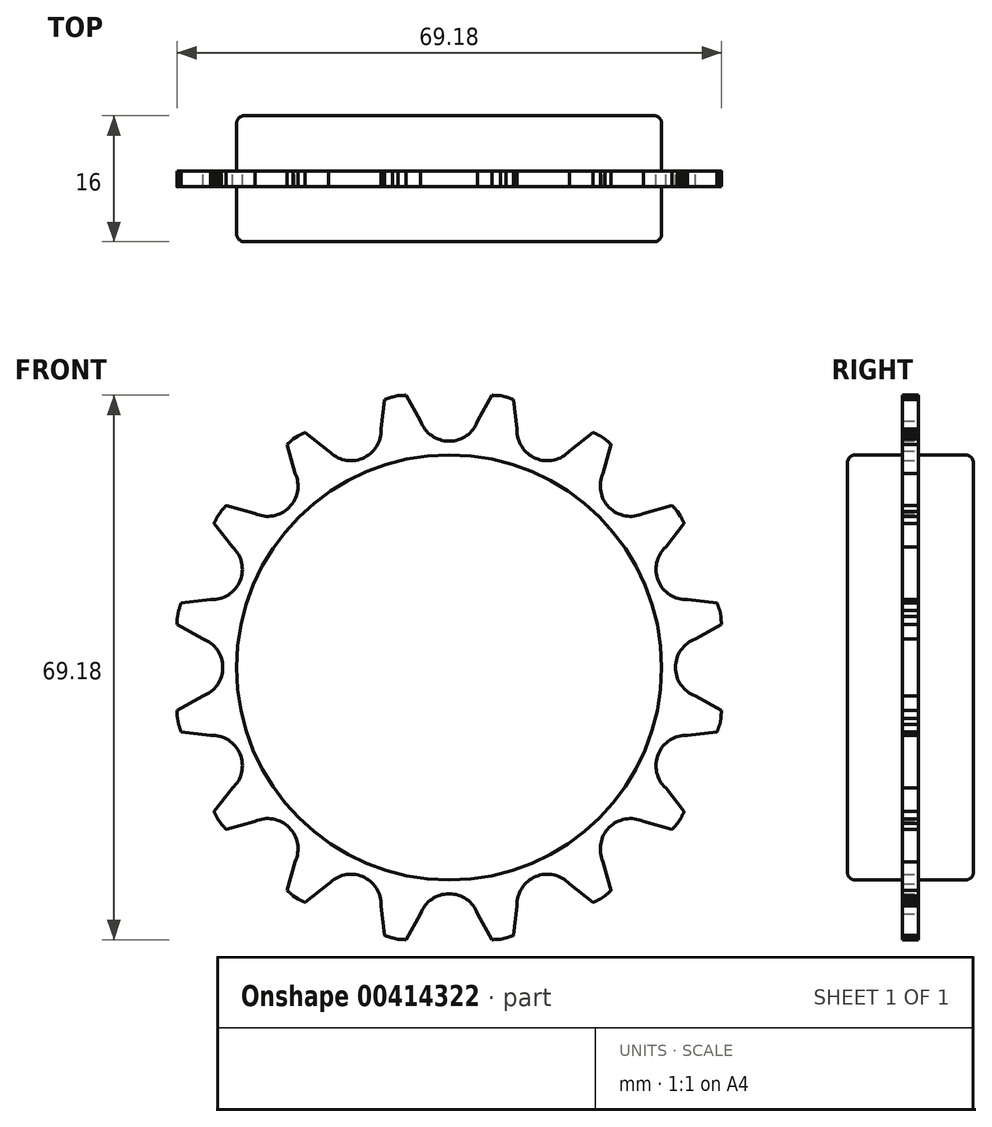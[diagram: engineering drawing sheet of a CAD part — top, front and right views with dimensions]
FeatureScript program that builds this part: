
annotation { "Feature Type Name" : "Feature", "Feature Type Description" : "" }
export const myFeature = defineFeature(function(context is Context, id is Id, definition is map)
    precondition{}
    {
        {
            var Q0;
            Q0=qCreatedBy(makeId("Front.planeOp"),FACE);
            var sketch = newSketch(context, id + "F0", { "sketchPlane" : qUnion([Q0])});
            skArc(sketch, "E0", {"start": v(-3.62, 31.28) * mm, "mid": v(0, 28.75) * mm, "end": v(3.62, 31.28) * mm});
            skPoint(sketch, "E1.center", {"position": v(0, -0.09) * mm});
            skArc(sketch, "E2.trimOffspring", {"start": v(6.5, 34.52) * mm, "mid": v(5.98, 34.55) * mm, "end": v(5.47, 34.59) * mm});
            skArc(sketch, "E3.1.5", {"start": v(-5.47, 34.59) * mm, "mid": v(-5.98, 34.55) * mm, "end": v(-6.5, 34.52) * mm});
            skLineSegment(sketch, "E4", {"start": v(3.62, 31.28) * mm, "end": v(5.47, 34.59) * mm});
            skLineSegment(sketch, "E5.MirrorCS", {"start": v(-3.62, 31.28) * mm, "end": v(-5.47, 34.59) * mm});
            skArc(sketch, "E6.1.0", {"start": v(-15.31, 27.51) * mm, "mid": v(-11, 26.56) * mm, "end": v(-8.63, 30.28) * mm});
            skLineSegment(sketch, "E6.1.1", {"start": v(-8.63, 30.28) * mm, "end": v(-8.18, 34.05) * mm});
            skArc(sketch, "E6.1.2", {"start": v(-7.21, 34.37) * mm, "mid": v(-7.7, 34.21) * mm, "end": v(-8.18, 34.05) * mm});
            skArc(sketch, "E6.1.3", {"start": v(-18.3, 29.86) * mm, "mid": v(-18.75, 29.63) * mm, "end": v(-19.2, 29.4) * mm});
            skLineSegment(sketch, "E6.1.4", {"start": v(-15.31, 27.51) * mm, "end": v(-18.3, 29.86) * mm});
            skArc(sketch, "E6.2.0", {"start": v(-24.67, 19.56) * mm, "mid": v(-20.33, 20.33) * mm, "end": v(-19.56, 24.67) * mm});
            skLineSegment(sketch, "E6.2.1", {"start": v(-19.56, 24.67) * mm, "end": v(-20.59, 28.33) * mm});
            skArc(sketch, "E6.2.2", {"start": v(-19.82, 29) * mm, "mid": v(-20.2, 28.66) * mm, "end": v(-20.59, 28.33) * mm});
            skArc(sketch, "E6.2.3", {"start": v(-28.33, 20.59) * mm, "mid": v(-28.66, 20.2) * mm, "end": v(-29, 19.82) * mm});
            skLineSegment(sketch, "E6.2.4", {"start": v(-24.67, 19.56) * mm, "end": v(-28.33, 20.59) * mm});
            skArc(sketch, "E6.3.0", {"start": v(-30.28, 8.63) * mm, "mid": v(-26.56, 11) * mm, "end": v(-27.51, 15.31) * mm});
            skLineSegment(sketch, "E6.3.1", {"start": v(-27.51, 15.31) * mm, "end": v(-29.86, 18.3) * mm});
            skArc(sketch, "E6.3.2", {"start": v(-29.4, 19.2) * mm, "mid": v(-29.63, 18.75) * mm, "end": v(-29.86, 18.3) * mm});
            skArc(sketch, "E6.3.3", {"start": v(-34.05, 8.18) * mm, "mid": v(-34.21, 7.7) * mm, "end": v(-34.37, 7.21) * mm});
            skLineSegment(sketch, "E6.3.4", {"start": v(-30.28, 8.63) * mm, "end": v(-34.05, 8.18) * mm});
            skArc(sketch, "E6.4.0", {"start": v(-31.28, -3.62) * mm, "mid": v(-28.75, 0) * mm, "end": v(-31.28, 3.62) * mm});
            skLineSegment(sketch, "E6.4.1", {"start": v(-31.28, 3.62) * mm, "end": v(-34.59, 5.47) * mm});
            skArc(sketch, "E6.4.2", {"start": v(-34.52, 6.5) * mm, "mid": v(-34.55, 5.98) * mm, "end": v(-34.59, 5.47) * mm});
            skArc(sketch, "E6.4.3", {"start": v(-34.59, -5.47) * mm, "mid": v(-34.55, -5.98) * mm, "end": v(-34.52, -6.5) * mm});
            skLineSegment(sketch, "E6.4.4", {"start": v(-31.28, -3.62) * mm, "end": v(-34.59, -5.47) * mm});
            skArc(sketch, "E6.5.0", {"start": v(-27.51, -15.31) * mm, "mid": v(-26.56, -11) * mm, "end": v(-30.28, -8.63) * mm});
            skLineSegment(sketch, "E6.5.1", {"start": v(-30.28, -8.63) * mm, "end": v(-34.05, -8.18) * mm});
            skArc(sketch, "E6.5.2", {"start": v(-34.37, -7.21) * mm, "mid": v(-34.21, -7.7) * mm, "end": v(-34.05, -8.18) * mm});
            skArc(sketch, "E6.5.3", {"start": v(-29.86, -18.3) * mm, "mid": v(-29.63, -18.75) * mm, "end": v(-29.4, -19.2) * mm});
            skLineSegment(sketch, "E6.5.4", {"start": v(-27.51, -15.31) * mm, "end": v(-29.86, -18.3) * mm});
            skArc(sketch, "E6.6.0", {"start": v(-19.56, -24.67) * mm, "mid": v(-20.33, -20.33) * mm, "end": v(-24.67, -19.56) * mm});
            skLineSegment(sketch, "E6.6.1", {"start": v(-24.67, -19.56) * mm, "end": v(-28.33, -20.59) * mm});
            skArc(sketch, "E6.6.2", {"start": v(-29, -19.82) * mm, "mid": v(-28.66, -20.2) * mm, "end": v(-28.33, -20.59) * mm});
            skArc(sketch, "E6.6.3", {"start": v(-20.59, -28.33) * mm, "mid": v(-20.2, -28.66) * mm, "end": v(-19.82, -29) * mm});
            skLineSegment(sketch, "E6.6.4", {"start": v(-19.56, -24.67) * mm, "end": v(-20.59, -28.33) * mm});
            skArc(sketch, "E6.7.0", {"start": v(-8.63, -30.28) * mm, "mid": v(-11, -26.56) * mm, "end": v(-15.31, -27.51) * mm});
            skLineSegment(sketch, "E6.7.1", {"start": v(-15.31, -27.51) * mm, "end": v(-18.3, -29.86) * mm});
            skArc(sketch, "E6.7.2", {"start": v(-19.2, -29.4) * mm, "mid": v(-18.75, -29.63) * mm, "end": v(-18.3, -29.86) * mm});
            skArc(sketch, "E6.7.3", {"start": v(-8.18, -34.05) * mm, "mid": v(-7.7, -34.21) * mm, "end": v(-7.21, -34.37) * mm});
            skLineSegment(sketch, "E6.7.4", {"start": v(-8.63, -30.28) * mm, "end": v(-8.18, -34.05) * mm});
            skArc(sketch, "E6.8.0", {"start": v(3.62, -31.28) * mm, "mid": v(0, -28.75) * mm, "end": v(-3.62, -31.28) * mm});
            skLineSegment(sketch, "E6.8.1", {"start": v(-3.62, -31.28) * mm, "end": v(-5.47, -34.59) * mm});
            skArc(sketch, "E6.8.2", {"start": v(-6.5, -34.52) * mm, "mid": v(-5.98, -34.55) * mm, "end": v(-5.47, -34.59) * mm});
            skArc(sketch, "E6.8.3", {"start": v(5.47, -34.59) * mm, "mid": v(5.98, -34.55) * mm, "end": v(6.5, -34.52) * mm});
            skLineSegment(sketch, "E6.8.4", {"start": v(3.62, -31.28) * mm, "end": v(5.47, -34.59) * mm});
            skArc(sketch, "E6.9.0", {"start": v(15.31, -27.51) * mm, "mid": v(11, -26.56) * mm, "end": v(8.63, -30.28) * mm});
            skLineSegment(sketch, "E6.9.1", {"start": v(8.63, -30.28) * mm, "end": v(8.18, -34.05) * mm});
            skArc(sketch, "E6.9.2", {"start": v(7.21, -34.37) * mm, "mid": v(7.7, -34.21) * mm, "end": v(8.18, -34.05) * mm});
            skArc(sketch, "E6.9.3", {"start": v(18.3, -29.86) * mm, "mid": v(18.75, -29.63) * mm, "end": v(19.2, -29.4) * mm});
            skLineSegment(sketch, "E6.9.4", {"start": v(15.31, -27.51) * mm, "end": v(18.3, -29.86) * mm});
            skArc(sketch, "E6.10.0", {"start": v(24.67, -19.56) * mm, "mid": v(20.33, -20.33) * mm, "end": v(19.56, -24.67) * mm});
            skLineSegment(sketch, "E6.10.1", {"start": v(19.56, -24.67) * mm, "end": v(20.59, -28.33) * mm});
            skArc(sketch, "E6.10.2", {"start": v(19.82, -29) * mm, "mid": v(20.2, -28.66) * mm, "end": v(20.59, -28.33) * mm});
            skArc(sketch, "E6.10.3", {"start": v(28.33, -20.59) * mm, "mid": v(28.66, -20.2) * mm, "end": v(29, -19.82) * mm});
            skLineSegment(sketch, "E6.10.4", {"start": v(24.67, -19.56) * mm, "end": v(28.33, -20.59) * mm});
            skArc(sketch, "E6.11.0", {"start": v(30.28, -8.63) * mm, "mid": v(26.56, -11) * mm, "end": v(27.51, -15.31) * mm});
            skLineSegment(sketch, "E6.11.1", {"start": v(27.51, -15.31) * mm, "end": v(29.86, -18.3) * mm});
            skArc(sketch, "E6.11.2", {"start": v(29.4, -19.2) * mm, "mid": v(29.63, -18.75) * mm, "end": v(29.86, -18.3) * mm});
            skArc(sketch, "E6.11.3", {"start": v(34.05, -8.18) * mm, "mid": v(34.21, -7.7) * mm, "end": v(34.37, -7.21) * mm});
            skLineSegment(sketch, "E6.11.4", {"start": v(30.28, -8.63) * mm, "end": v(34.05, -8.18) * mm});
            skArc(sketch, "E6.12.0", {"start": v(31.28, 3.62) * mm, "mid": v(28.75, 0) * mm, "end": v(31.28, -3.62) * mm});
            skLineSegment(sketch, "E6.12.1", {"start": v(31.28, -3.62) * mm, "end": v(34.59, -5.47) * mm});
            skArc(sketch, "E6.12.2", {"start": v(34.52, -6.5) * mm, "mid": v(34.55, -5.98) * mm, "end": v(34.59, -5.47) * mm});
            skArc(sketch, "E6.12.3", {"start": v(34.59, 5.47) * mm, "mid": v(34.55, 5.98) * mm, "end": v(34.52, 6.5) * mm});
            skLineSegment(sketch, "E6.12.4", {"start": v(31.28, 3.62) * mm, "end": v(34.59, 5.47) * mm});
            skArc(sketch, "E6.13.0", {"start": v(27.51, 15.31) * mm, "mid": v(26.56, 11) * mm, "end": v(30.28, 8.63) * mm});
            skLineSegment(sketch, "E6.13.1", {"start": v(30.28, 8.63) * mm, "end": v(34.05, 8.18) * mm});
            skArc(sketch, "E6.13.2", {"start": v(34.37, 7.21) * mm, "mid": v(34.21, 7.7) * mm, "end": v(34.05, 8.18) * mm});
            skArc(sketch, "E6.13.3", {"start": v(29.86, 18.3) * mm, "mid": v(29.63, 18.75) * mm, "end": v(29.4, 19.2) * mm});
            skLineSegment(sketch, "E6.13.4", {"start": v(27.51, 15.31) * mm, "end": v(29.86, 18.3) * mm});
            skArc(sketch, "E6.14.0", {"start": v(19.56, 24.67) * mm, "mid": v(20.33, 20.33) * mm, "end": v(24.67, 19.56) * mm});
            skLineSegment(sketch, "E6.14.1", {"start": v(24.67, 19.56) * mm, "end": v(28.33, 20.59) * mm});
            skArc(sketch, "E6.14.2", {"start": v(29, 19.82) * mm, "mid": v(28.66, 20.2) * mm, "end": v(28.33, 20.59) * mm});
            skArc(sketch, "E6.14.3", {"start": v(20.59, 28.33) * mm, "mid": v(20.2, 28.66) * mm, "end": v(19.82, 29) * mm});
            skLineSegment(sketch, "E6.14.4", {"start": v(19.56, 24.67) * mm, "end": v(20.59, 28.33) * mm});
            skArc(sketch, "E6.15.0", {"start": v(8.63, 30.28) * mm, "mid": v(11, 26.56) * mm, "end": v(15.31, 27.51) * mm});
            skLineSegment(sketch, "E6.15.1", {"start": v(15.31, 27.51) * mm, "end": v(18.3, 29.86) * mm});
            skArc(sketch, "E6.15.2", {"start": v(19.2, 29.4) * mm, "mid": v(18.75, 29.63) * mm, "end": v(18.3, 29.86) * mm});
            skArc(sketch, "E6.15.3", {"start": v(8.18, 34.05) * mm, "mid": v(7.7, 34.21) * mm, "end": v(7.21, 34.37) * mm});
            skLineSegment(sketch, "E6.15.4", {"start": v(8.63, 30.28) * mm, "end": v(8.18, 34.05) * mm});
            skPoint(sketch, "E6.center", {"position": v(0, 0) * mm});
            skCircle(sketch, "E7", {"center": v(0, 0) * mm, "radius": 27 * mm});
            skLineSegment(sketch, "E8", {"start": v(6.5, 34.52) * mm, "end": v(7.21, 34.37) * mm});
            skLineSegment(sketch, "E9", {"start": v(19.2, 29.4) * mm, "end": v(19.82, 29) * mm});
            skLineSegment(sketch, "E10", {"start": v(29, 19.82) * mm, "end": v(29.4, 19.2) * mm});
            skLineSegment(sketch, "E11", {"start": v(34.37, 7.21) * mm, "end": v(34.52, 6.5) * mm});
            skLineSegment(sketch, "E12", {"start": v(34.52, -6.5) * mm, "end": v(34.37, -7.21) * mm});
            skLineSegment(sketch, "E13", {"start": v(29.4, -19.2) * mm, "end": v(29, -19.82) * mm});
            skLineSegment(sketch, "E14", {"start": v(19.82, -29) * mm, "end": v(19.2, -29.4) * mm});
            skLineSegment(sketch, "E15", {"start": v(7.21, -34.37) * mm, "end": v(6.5, -34.52) * mm});
            skLineSegment(sketch, "E16", {"start": v(-6.5, -34.52) * mm, "end": v(-7.21, -34.37) * mm});
            skLineSegment(sketch, "E17", {"start": v(-19.2, -29.4) * mm, "end": v(-19.82, -29) * mm});
            skLineSegment(sketch, "E18", {"start": v(-29, -19.82) * mm, "end": v(-29.4, -19.2) * mm});
            skLineSegment(sketch, "E19", {"start": v(-34.37, -7.21) * mm, "end": v(-34.52, -6.5) * mm});
            skLineSegment(sketch, "E20", {"start": v(-34.52, 6.5) * mm, "end": v(-34.37, 7.21) * mm});
            skLineSegment(sketch, "E21", {"start": v(-29.4, 19.2) * mm, "end": v(-29, 19.82) * mm});
            skLineSegment(sketch, "E22", {"start": v(-19.82, 29) * mm, "end": v(-19.2, 29.4) * mm});
            skLineSegment(sketch, "E23", {"start": v(-7.21, 34.37) * mm, "end": v(-6.5, 34.52) * mm});
            skSolve(sketch);
        }
        {
            var Q0;
            Q0=makeQuery(id+"F0.imprint","IMPRINT",FACE,{"disambiguationData":[TD([[makeQuery(id+"F0.imprint","IMPRINT",EDGE,{"derivedFrom":sQuery(id+"F0.wireOp",EDGE,"E0")}),-1.0]])]});
            extrude(context, id + "F1", {"entities" : qUnion([Q0]), "endBound" : BoundingType.SYMMETRIC, "depth" : 2 * mm});
        }
        {
            var Q0;
            Q0=makeQuery(id+"F0.imprint","IMPRINT",FACE,{"disambiguationData":[TD([[makeQuery(id+"F0.imprint","IMPRINT",EDGE,{"derivedFrom":sQuery(id+"F0.wireOp",EDGE,"E7")}),1.0]])]});
            extrude(context, id + "F2", {"entities" : qUnion([Q0]), "operationType" : NewBodyOperationType.ADD, "endBound" : BoundingType.SYMMETRIC, "depth" : 16 * mm});
        }
        {
            var Q0;
            Q0=makeQuery(id+"F2.opExtrude","CAP_EDGE",EDGE,{"disambiguationData":[OSD([sQuery(id+"F0.wireOp",EDGE,"E7")])],"isStart":false});
            var Q1;
            Q1=makeQuery(id+"F2.opExtrude","CAP_EDGE",EDGE,{"disambiguationData":[OSD([sQuery(id+"F0.wireOp",EDGE,"E7")])],"isStart":true});
            fillet(context, id + "F3", {"entities" : qUnion([Q0, Q1]), "radius" : 1 * mm, "tangentPropagation" : true, "allowEdgeOverflow" : false});
        }
    });
